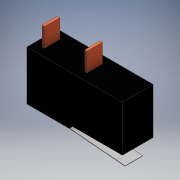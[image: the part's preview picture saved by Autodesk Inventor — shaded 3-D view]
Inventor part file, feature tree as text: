
AUTODESK INVENTOR PART (.ipt)
format: ipt  version: 2016 (Build 200138000, 138)  size: 135,168 bytes
history: native  units: mm
features: extrude x3, sketch x3, plane x1
ambient origin geometry x8: Origin, YZ Plane, XZ Plane, XY Plane, X Axis, Y Axis, Z Axis, Center Point
bodies: Solid1 (feature_tree)
feature tree (7):
  extrude  "Extrusion1"  Depth=9.5mm
  extrude  "Extrusion2"  TaperAngle=135.0deg  [1 undecoded]
  plane  "Work Plane1"
  extrude  "Extrusion3"  Depth=0.46mm
  sketch  "Sketch1"  dims[d0=10.2mm d1=9.5mm]
  sketch  "Sketch2"  dims[d4=8.8mm d5=135.0deg]
  sketch  "Sketch3"  dims[d7=0.0mm d8=0.46mm d10=1.6mm d11=8.8mm d12=1.6mm d13=3.9mm d14=0.0mm d15=16.0mm d16=1.0mm d17=0.1mm d18=0.1mm d19=16.580628mm d20=3.0mm d21=3.6mm d22=0.0mm]
note: 1 required parameter value undecoded (feature->parameter linkage not recoverable at this tier; creation-order binding heuristic only, values carry confidence <= 0.55)
